# Revit family: KEUCO_14911010000
name_source: partatom
category: Allgemeines Modell
revit_build: Autodesk Revit 2016 (Build: 20150220_1215(x64)
units: mm (PartAtom-declared; Revit-internal decimal feet)

## family parameters
Arbeitsebenenbasiert = Ja
Beim Laden mit Abzugskörper schneiden = Nein
Bemaßung runder Anschluss = Durchmesser verwenden
Gemeinsam genutzt = Nein
Immer vertikal = Nein
Kann Basisbauteil für Bewehrung sein = Nein
Raumberechnungspunkt = Nein
Teiletyp = Normal

## types (3) — shared parameters
Hersteller = KEUCO
Material Haken = ABS Kunststoff - Schwarz
Serie = Plan
Stange Breite = 89 mm  [stored 0.291995 ft]
URL = https://www.keuco.com
Verwendung = WP
Vorgabe-Ansicht = 1219 mm
zero-valued in all types: Gewicht

## per-type parameters (varying)
| type | Ausschreibungstext | Material |
| 14911010000 | KEUCO PLAN Handtuchhaken 14911010000 mit Türpuffer
Hochglanzverchromter Handtuchhaken in ästhetischem, funktionalem Design
Abschlussstück aus schwarzem ABS Kunststoff als Türpuffer
runde Rosettenkappe, Durchmesser 55 mm
leicht zu reinigen
Ausladung 91 mm
Der Handtuchhaken wird verdeckt angebracht
Lieferung inkl. korrosionsfreiem Befestigungsmaterial | Aluminium silber-eloxiert (E6 EV1) |
| 14911070000 | KEUCO PLAN Handtuchhaken 14911070000 mit Türpuffer
Zeitloser Handtuchhaken aus hochwertigem Edelstahl
in ästhetischem, funktionalem Design
Abschlussstück aus schwarzem ABS Kunststoff als Türpuffer
runde Rosettenkappe, Durchmesser 55 mm
leicht zu reinigen
Ausladung 91 mm
Der Handtuchhaken wird verdeckt angebracht
Lieferung inkl. korrosionsfreiem Befestigungsmaterial | Edelstahl |
| 14911170000 | KEUCO PLAN Handtuchhaken 14911170000 mit Türpuffer
Handtuchhaken aus silber-eloxiertem Aluminium (E6 EV1) 
in ästhetischem, funktionalem Design
Abschlussstück aus schwarzem ABS Kunststoff als Türpuffer
runde Rosettenkappe, Durchmesser 55 mm
leicht zu reinigen
Ausladung 91 mm
Der Handtuchhaken wird verdeckt angebracht
Lieferung inkl. korrosionsfreiem Befestigungsmaterial | Aluminium silber-eloxiert (E6 EV1) |

note: column(s) folded — value = type name in every type: Artikelnummer

note: [stored X ft] marks values corroborated as IEEE doubles in the binary element streams (Revit-internal decimal feet)

## geometry (parser evidence)
native form markers: Blend x9, Sweep x3
no freeform markers — native parametric forms only
